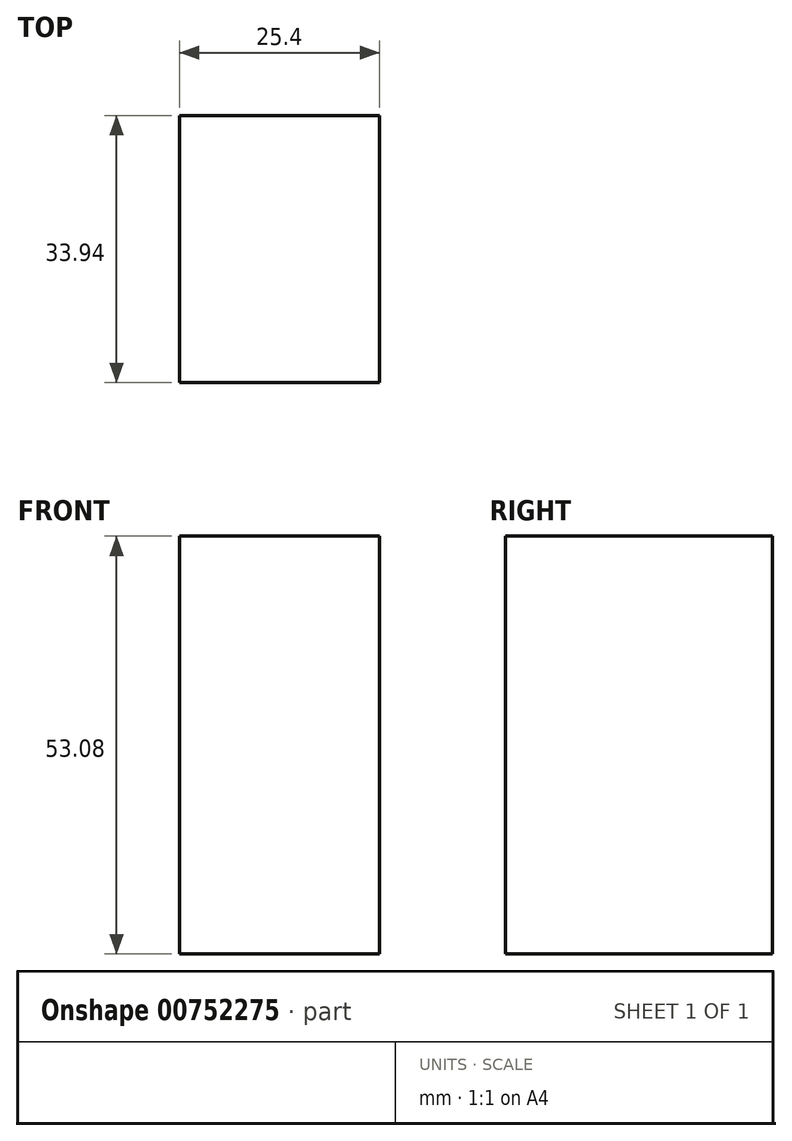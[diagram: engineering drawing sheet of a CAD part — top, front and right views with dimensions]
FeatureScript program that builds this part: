
annotation { "Feature Type Name" : "Feature", "Feature Type Description" : "" }
export const myFeature = defineFeature(function(context is Context, id is Id, definition is map)
    precondition{}
    {
        {
            var Q0;
            Q0=qCreatedBy(makeId("Right.planeOp"),FACE);
            var sketch = newSketch(context, id + "F0", { "sketchPlane" : qUnion([Q0])});
            skLineSegment(sketch, "E0.bottom", {"start": v(0, 24.14) * mm, "end": v(33.94, 24.14) * mm});
            skLineSegment(sketch, "E0.top", {"start": v(0, -28.94) * mm, "end": v(33.94, -28.94) * mm});
            skLineSegment(sketch, "E0.left", {"start": v(0, 24.14) * mm, "end": v(0, -28.94) * mm});
            skLineSegment(sketch, "E0.right", {"start": v(33.94, 24.14) * mm, "end": v(33.94, -28.94) * mm});
            skSolve(sketch);
        }
        {
            var Q0;
            Q0 = qSketchRegion(id + "F0", true);
            extrude(context, id + "F1", {"entities" : qUnion([Q0]), "depth" : 25.4 * mm, "offsetDistance" : 25.4 * mm});
        }
        {
            var Q0;
            Q0=makeQuery(id+"F1.opExtrude","CAP_FACE",FACE,{"disambiguationData":[OSD([sQuery(id+"F0.wireOp",EDGE,"E0.bottom"),sQuery(id+"F0.wireOp",EDGE,"E0.top"),sQuery(id+"F0.wireOp",EDGE,"E0.left"),sQuery(id+"F0.wireOp",EDGE,"E0.right")])],"isStart":false});
            var sketch = newSketch(context, id + "F2", { "sketchPlane" : qUnion([Q0])});
            skSolve(sketch);
        }
        {
            var Q0;
            Q0=makeQuery(id+"F2.imprint","IMPRINT",FACE,{"disambiguationData":[TD([[makeQuery(id+"F2.imprint","IMPRINT",EDGE,{"derivedFrom":makeQuery(id+"F1.opExtrude","CAP_EDGE",EDGE,{"disambiguationData":[OSD([sQuery(id+"F0.wireOp",EDGE,"E0.bottom")])],"isStart":false})}),-1.0]])]});
            var sketch = newSketch(context, id + "F3", { "sketchPlane" : qUnion([Q0])});
            skCircle(sketch, "E1", {"center": v(17.94, 0) * mm, "radius": 18.86 * mm});
            skSolve(sketch);
        }
        {
            var Q0;
            Q0=sQuery(id+"F3.wireOp",EDGE,"E1");
            extrude(context, id + "F4", {"bodyType" : ToolBodyType.SURFACE, "surfaceEntities" : qUnion([Q0]), "depth" : 25.4 * mm, "offsetDistance" : 25.4 * mm});
        }
    });
